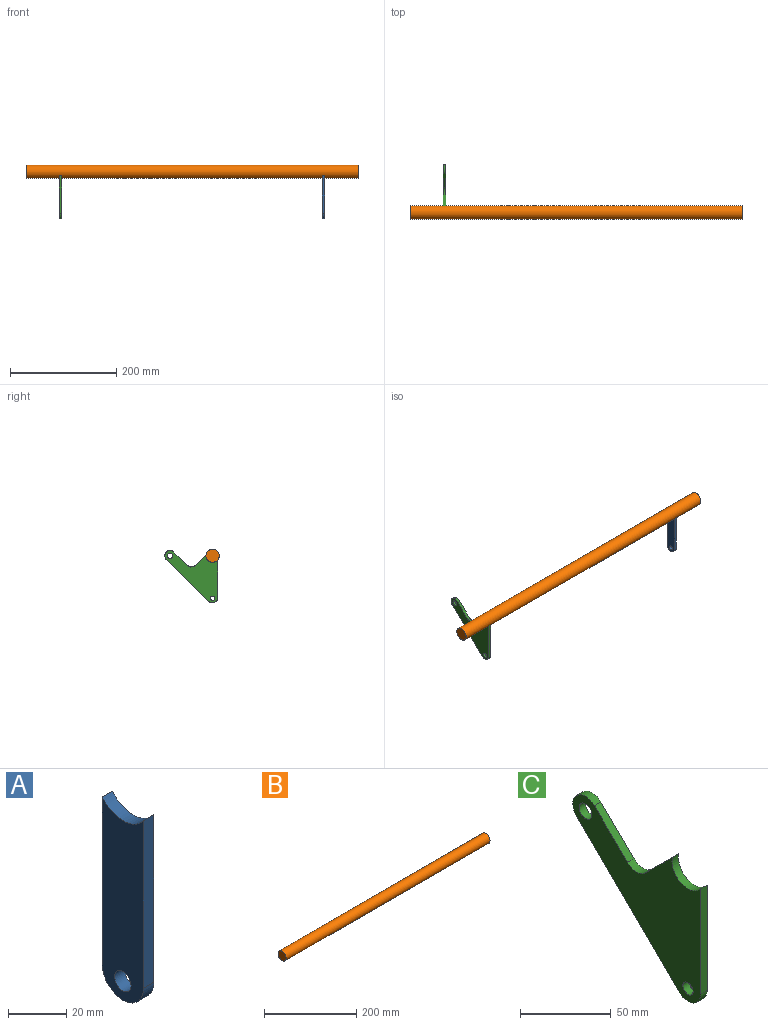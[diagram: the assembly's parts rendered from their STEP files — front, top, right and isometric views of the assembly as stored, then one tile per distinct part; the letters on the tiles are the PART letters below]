
ASSEMBLY  parts=3 mates=2
PART A: 7 faces, bbox 5x20x80.5 mm
  f0: cylinder r=12.5mm len=20mm, axis (-1,0,0), area 115.9mm2, adj f1,f3,f5,f6
  f1: plane 70.5x5mm, normal (0,-1,0), area 352.5mm2, adj f0,f2,f5,f6
  f2: cylinder r=10mm len=20mm, axis (-1,0,0), area 157.1mm2, adj f1,f3,f5,f6
  f3: plane 70.5x5mm, normal (0,1,0), area 352.5mm2, adj f0,f2,f5,f6
  f4: cylinder r=4mm len=8mm, axis (-1,0,0), area 125.7mm2, adj f5,f6
  f5: plane 80.5x20mm, normal (1,0,0), area 1446.9mm2, adj f0,f1,f2,f3,f4
  f6: plane 80.5x20mm, normal (-1,0,0), area 1446.9mm2, adj f0,f1,f2,f3,f4
PART B: 3 faces, bbox 625x25x25 mm
  f0: cylinder r=12.5mm len=625mm, axis (-1,0,0), area 49087.4mm2, adj f1,f2
  f1: plane 25x25mm, normal (1,0,0), area 490.9mm2, adj f0
  f2: plane 25x25mm, normal (-1,0,0), area 490.9mm2, adj f0
PART C: 12 faces, bbox 5x100x98.6 mm
  f0: cylinder r=12.5mm len=22.5mm, axis (-1,0,0), area 169.4mm2, adj f1,f8,f10,f11
  f1: plane 71.1x5mm, normal (0,-1,0), area 355.5mm2, adj f0,f2,f10,f11
  f2: cylinder r=10mm len=17.01mm, axis (-1,0,0), area 117.4mm2, adj f1,f3,f10,f11
  f3: plane 80x78.6mm, normal (0,0.7,-0.71), area 560.8mm2, adj f2,f4,f10,f11
  f4: cylinder r=10mm len=17.13mm, axis (-1,0,0), area 157.1mm2, adj f3,f5,f10,f11
  f5: plane 25.85x25.4mm, normal (0,-0.7,0.71), area 181.2mm2, adj f4,f6,f10,f11
  f6: cylinder r=10mm len=14.08mm, axis (-1,0,0), area 78.1mm2, adj f5,f8,f10,f11
  f7: cylinder r=4mm len=8mm, axis (-1,0,0), area 125.7mm2, adj f10,f11
  f8: plane 20.84x20.84mm, normal (0,0.71,0.71), area 147.4mm2, adj f0,f6,f10,f11
  f9: cylinder r=5mm len=10mm, axis (-1,0,0), area 157.1mm2, adj f10,f11
  f10: plane 100x98.6mm, normal (1,0,0), area 4397.9mm2, adj f0,f1,f2,f3,f4,f5,f6,f7
  f11: plane 100x98.6mm, normal (-1,0,0), area 4397.9mm2, adj f0,f1,f2,f3,f4,f5,f6,f7
PLACE A t=(131.96,97.98,-3.65)mm
PLACE B t=(-425.54,431.81,-9.46)mm
PLACE C t=(-363.04,54.78,11.85)mm
MATE fastened C.f0 <-> B.f0  axis (1,0,0) through (-358.04,-106.84,-62.37)mm
MATE fastened A.f0 <-> B.f0  axis (1,0,0) through (136.96,-106.84,-62.37)mm
